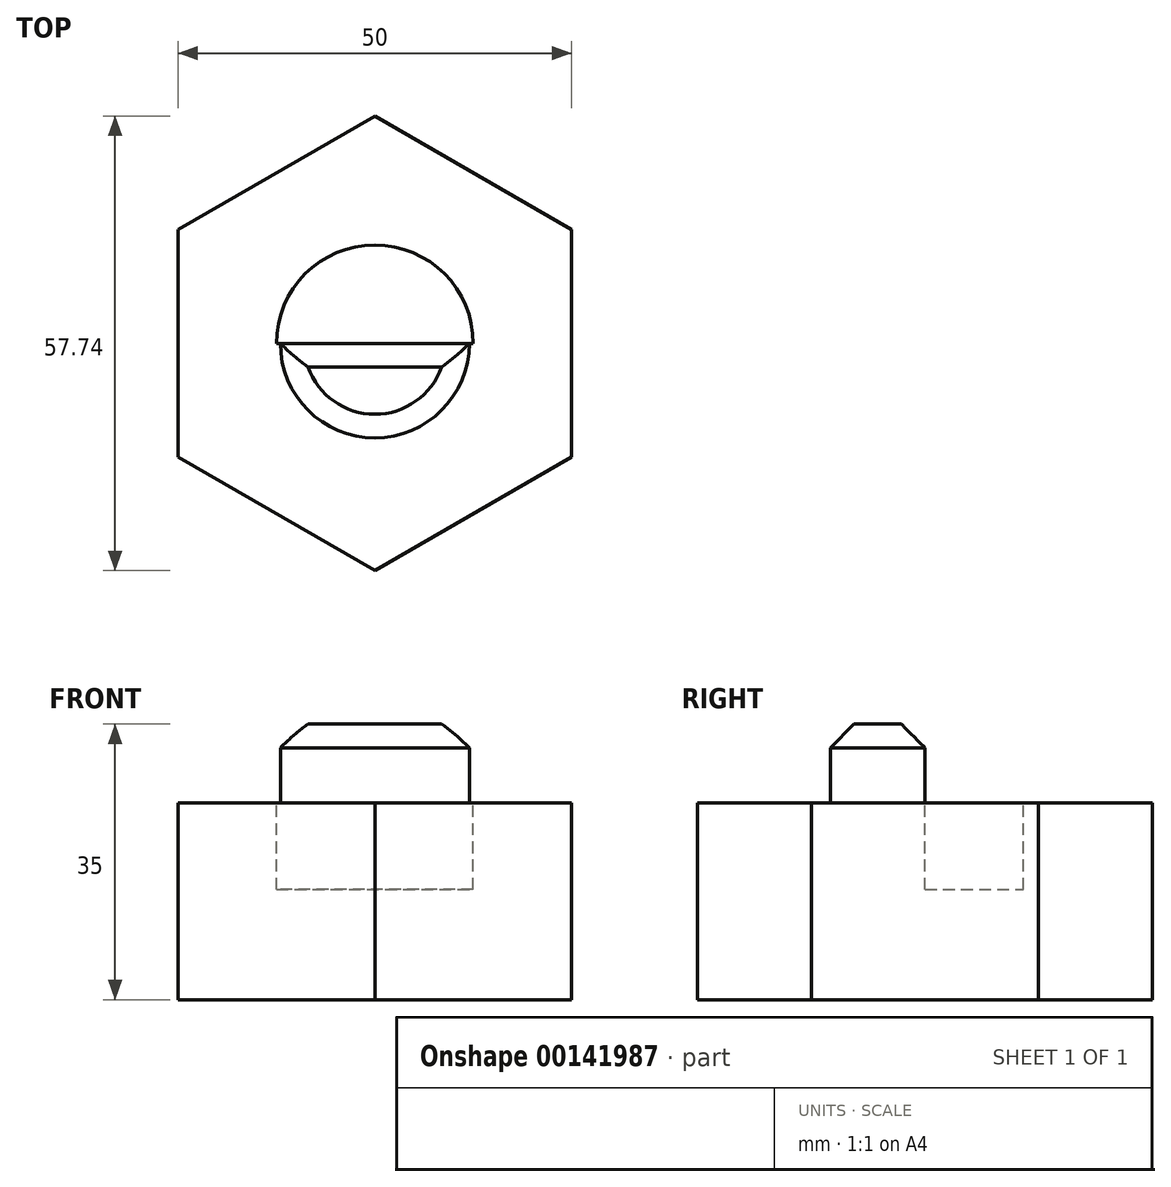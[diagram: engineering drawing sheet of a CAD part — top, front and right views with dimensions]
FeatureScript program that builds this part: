
annotation { "Feature Type Name" : "Feature", "Feature Type Description" : "" }
export const myFeature = defineFeature(function(context is Context, id is Id, definition is map)
    precondition{}
    {
        {
            var Q0;
            Q0=qCreatedBy(makeId("Top.planeOp"),FACE);
            var sketch = newSketch(context, id + "F0", { "sketchPlane" : qUnion([Q0])});
            skCircle(sketch, "E0.cCircle", {"center": v(0, 0) * mm, "radius": 25 * mm, "construction": true});
            skLineSegment(sketch, "E0.0", {"start": v(-25, -14.43) * mm, "end": v(-25, 14.43) * mm});
            skLineSegment(sketch, "E0.1", {"start": v(-25, 14.43) * mm, "end": v(0, 28.87) * mm});
            skLineSegment(sketch, "E0.2", {"start": v(0, 28.87) * mm, "end": v(25, 14.43) * mm});
            skLineSegment(sketch, "E0.3", {"start": v(25, 14.43) * mm, "end": v(25, -14.43) * mm});
            skLineSegment(sketch, "E0.4", {"start": v(25, -14.43) * mm, "end": v(0, -28.87) * mm});
            skLineSegment(sketch, "E0.5", {"start": v(0, -28.87) * mm, "end": v(-25, -14.43) * mm});
            skPoint(sketch, "E0.0.midPoint", {"position": v(-25, 0) * mm});
            skSolve(sketch);
        }
        {
            var Q0;
            Q0 = qSketchRegion(id + "F0", true);
            extrude(context, id + "F1", {"entities" : qUnion([Q0]), "depth" : 25 * mm});
        }
        {
            var Q0;
            Q0=makeQuery(id+"F1.opExtrude","CAP_FACE",FACE,{"disambiguationData":[OSD([sQuery(id+"F0.wireOp",EDGE,"E0.0"),sQuery(id+"F0.wireOp",EDGE,"E0.1"),sQuery(id+"F0.wireOp",EDGE,"E0.2"),sQuery(id+"F0.wireOp",EDGE,"E0.3"),sQuery(id+"F0.wireOp",EDGE,"E0.4"),sQuery(id+"F0.wireOp",EDGE,"E0.5")])],"isStart":false});
            var sketch = newSketch(context, id + "F2", { "sketchPlane" : qUnion([Q0])});
            skCircle(sketch, "E1", {"center": v(0, 0) * mm, "radius": 12 * mm});
            skLineSegment(sketch, "E2", {"start": v(-12, 0) * mm, "end": v(12, 0) * mm});
            skSolve(sketch);
        }
        {
            var Q0;
            {var subQ0=sQuery(id+"F2.wireOp",EDGE,"E2");Q0=makeQuery(id+"F2.imprint","IMPRINT",FACE,{"disambiguationData":[TD([[makeQuery(id+"F2.imprint","IMPRINT",EDGE,{"derivedFrom":subQ0}),-1.0]])]});}
            extrude(context, id + "F3", {"entities" : qUnion([Q0]), "operationType" : NewBodyOperationType.ADD, "depth" : 10 * mm});
        }
        {
            var Q0;
            Q0=makeQuery(id+"F3.opExtrude","CAP_EDGE",EDGE,{"disambiguationData":[OSD([sQuery(id+"F2.wireOp",EDGE,"E2")])],"isStart":false});
            var Q1;
            Q1=makeQuery(id+"F3.opExtrude","CAP_EDGE",EDGE,{"disambiguationData":[OSD([sQuery(id+"F2.wireOp",EDGE,"E1")])],"isStart":false});
            chamfer(context, id + "F4", {"entities" : qUnion([Q0, Q1]), "width" : 3 * mm, "tangentPropagation" : true});
        }
        {
            var Q0;
            Q0=makeQuery(id+"F2.imprint","IMPRINT",FACE,{"disambiguationData":[TD([[makeQuery(id+"F2.imprint","IMPRINT",EDGE,{"derivedFrom":makeQuery(id+"F1.opExtrude","CAP_EDGE",EDGE,{"disambiguationData":[OSD([sQuery(id+"F0.wireOp",EDGE,"E0.0")])],"isStart":false})}),-1.0]])]});
            var sketch = newSketch(context, id + "F5", { "sketchPlane" : qUnion([Q0])});
            skArc(sketch, "E3.0", {"start": v(12.49, -0.5) * mm, "mid": v(0, 12.5) * mm, "end": v(-12.49, -0.5) * mm});
            skLineSegment(sketch, "E3.1", {"start": v(-12.49, -0.5) * mm, "end": v(12.49, -0.5) * mm});
            skLineSegment(sketch, "E4", {"start": v(0, 0) * mm, "end": v(-12.5, 0) * mm});
            skLineSegment(sketch, "E5", {"start": v(0, 0) * mm, "end": v(12.5, 0) * mm});
            skSolve(sketch);
        }
        {
            var Q0;
            {var subQ0=sQuery(id+"F5.wireOp",EDGE,"E4");var subQ1=sQuery(id+"F5.wireOp",EDGE,"E3.0");var subQ2=makeQuery(id+"F5.imprint","INTERSECT",VERTEX,{"derivedFrom":[subQ1,subQ0]});Q0=makeQuery(id+"F5.imprint","IMPRINT",FACE,{"disambiguationData":[TD([[makeQuery(id+"F5.imprint","IMPRINT",EDGE,{"disambiguationData":[TD([[subQ2,1.0]])],"derivedFrom":subQ1}),1.0]])]});}
            var Q1;
            {var subQ0=sQuery(id+"F2.wireOp",EDGE,"E2");Q1=makeQuery(id+"F2.imprint","IMPRINT",FACE,{"disambiguationData":[TD([[makeQuery(id+"F2.imprint","IMPRINT",EDGE,{"derivedFrom":subQ0}),1.0]])]});}
            extrude(context, id + "F6", {"entities" : qUnion([Q0, Q1]), "operationType" : NewBodyOperationType.REMOVE, "oppositeDirection" : true, "depth" : 11 * mm});
        }
    });
